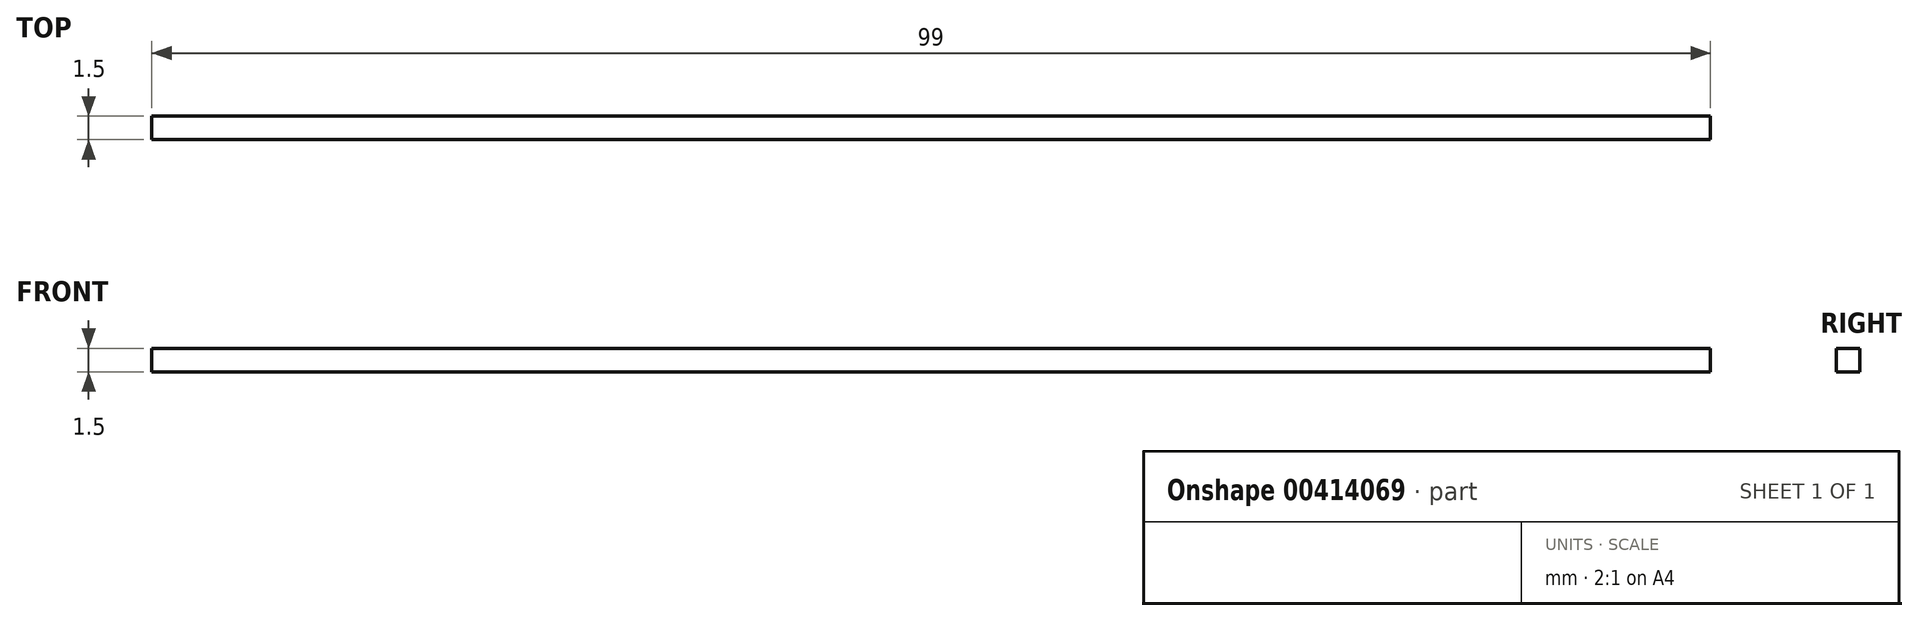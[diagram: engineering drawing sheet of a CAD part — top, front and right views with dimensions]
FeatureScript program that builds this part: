
annotation { "Feature Type Name" : "Feature", "Feature Type Description" : "" }
export const myFeature = defineFeature(function(context is Context, id is Id, definition is map)
    precondition{}
    {
        {
            var Q0;
            Q0=qCreatedBy(makeId("Top.planeOp"),FACE);
            var sketch = newSketch(context, id + "F0", { "sketchPlane" : qUnion([Q0])});
            skLineSegment(sketch, "E0.bottom", {"start": v(0, 0) * mm, "end": v(99, 0) * mm});
            skLineSegment(sketch, "E0.top", {"start": v(0, 1.5) * mm, "end": v(99, 1.5) * mm});
            skLineSegment(sketch, "E0.left", {"start": v(0, 0) * mm, "end": v(0, 1.5) * mm});
            skLineSegment(sketch, "E0.right", {"start": v(99, 0) * mm, "end": v(99, 1.5) * mm});
            skSolve(sketch);
        }
        {
            var Q0;
            Q0=makeQuery(id+"F0.imprint","IMPRINT",FACE,{"disambiguationData":[TD([[makeQuery(id+"F0.imprint","IMPRINT",EDGE,{"derivedFrom":sQuery(id+"F0.wireOp",EDGE,"E0.bottom")}),1.0]])]});
            extrude(context, id + "F1", {"entities" : qUnion([Q0]), "depth" : 1.5 * mm});
        }
    });
